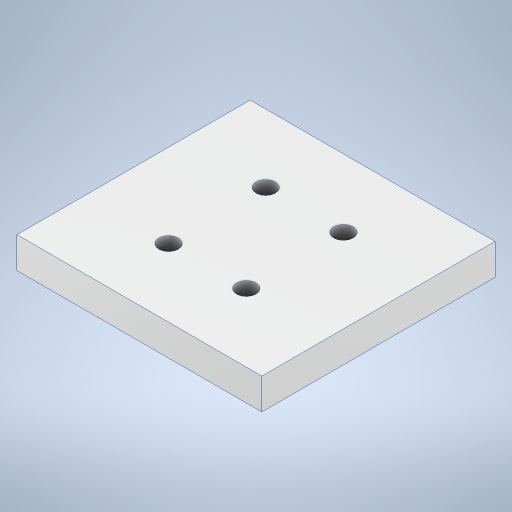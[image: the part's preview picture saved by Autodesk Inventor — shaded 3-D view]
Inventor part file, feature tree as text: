
AUTODESK INVENTOR PART (.ipt)
format: ipt  version: 2023 (Build 270158000, 158)  size: 249,856 bytes
history: native  units: mm
features: other x3, sketch x2, extrude x1, hole x1
ambient origin geometry x8: Origin, YZ Plane, XZ Plane, XY Plane, X Axis, Y Axis, Z Axis, Center Point
bodies: Body1 (feature_tree)
feature tree (7):
  extrude  "Extrusion2"  Depth=63.0mm
  hole  "Hole3"  [1 undecoded]
  sketch  "Sketch5"  dims[d43=53.25mm d68=63.0mm]
  sketch  "Sketch6"  dims[d69=60.0mm d70=8.0mm d71=0.0mm d72=20.0mm d74=25.0mm d75=20.0mm d77=20.0mm d80=63.0mm d81=60.0mm d82=21.5mm d83=17.5mm d84=5.0mm d85=6.0mm d86=4.0mm d87=2.0mm d88=90.0deg d89=5.0mm d90=20.594885mm d0=0.0mm d1=10.0mm d2=73.0mm]
  other  "Definição1"
  other  "Annotations"
  other  "Linear Dimension 1"
note: 1 required parameter value undecoded (feature->parameter linkage not recoverable at this tier; creation-order binding heuristic only, values carry confidence <= 0.55)
